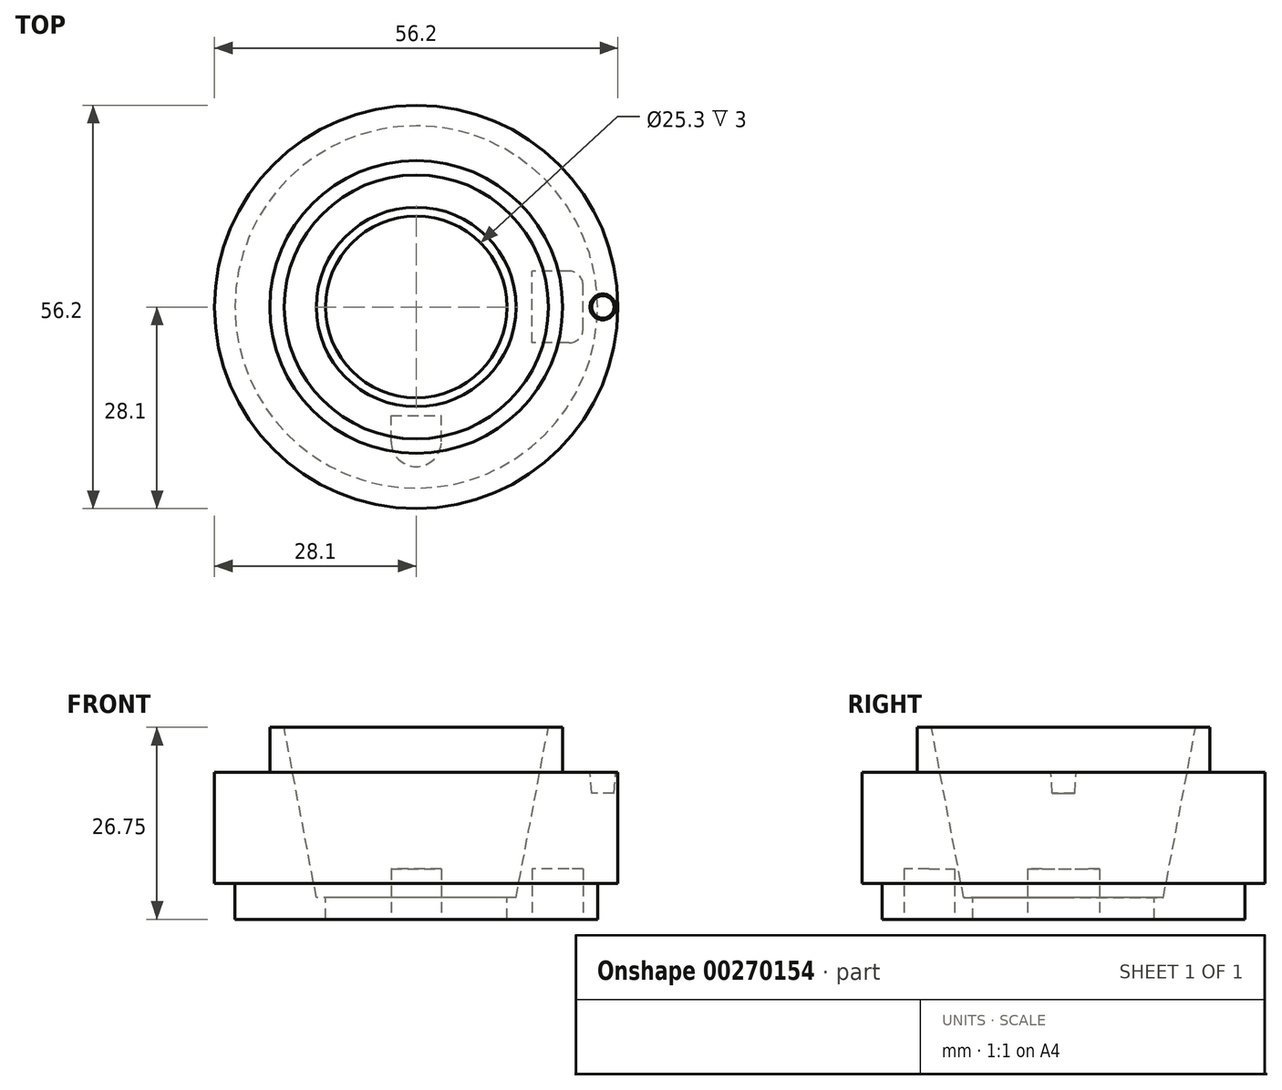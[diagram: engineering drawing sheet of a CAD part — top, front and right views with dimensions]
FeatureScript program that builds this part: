
annotation { "Feature Type Name" : "Feature", "Feature Type Description" : "" }
export const myFeature = defineFeature(function(context is Context, id is Id, definition is map)
    precondition{}
    {
        {
            var Q0;
            Q0=qCreatedBy(makeId("Front.planeOp"),FACE);
            var sketch = newSketch(context, id + "F0", { "sketchPlane" : qUnion([Q0])});
            skLineSegment(sketch, "E0", {"start": v(0, 18.35) * mm, "end": v(0, -26.13) * mm, "construction": true});
            skLineSegment(sketch, "E1", {"start": v(0, 0) * mm, "end": v(34.76, 0) * mm, "construction": true});
            skLineSegment(sketch, "E2", {"start": v(25.25, -40) * mm, "end": v(12.65, -40) * mm});
            skLineSegment(sketch, "E3", {"start": v(28.1, -19.5) * mm, "end": v(20.4, -19.5) * mm});
            skLineSegment(sketch, "E4", {"start": v(12.65, -40) * mm, "end": v(12.65, -37) * mm});
            skLineSegment(sketch, "E5", {"start": v(20.4, -19.5) * mm, "end": v(20.4, -13.25) * mm});
            skLineSegment(sketch, "E6", {"start": v(20.4, -13.25) * mm, "end": v(18.4, -13.25) * mm});
            skLineSegment(sketch, "E7", {"start": v(12.65, -37) * mm, "end": v(13.9, -37) * mm});
            skLineSegment(sketch, "E8", {"start": v(13.9, -37) * mm, "end": v(18.4, -13.25) * mm});
            skLineSegment(sketch, "E9", {"start": v(26, -10.98) * mm, "end": v(26, -23.61) * mm, "construction": true});
            skLineSegment(sketch, "E10", {"start": v(28.1, -19.5) * mm, "end": v(28.1, -35) * mm});
            skLineSegment(sketch, "E11", {"start": v(25.25, -40) * mm, "end": v(25.25, -35) * mm});
            skLineSegment(sketch, "E12", {"start": v(25.25, -35) * mm, "end": v(28.1, -35) * mm});
            skSolve(sketch);
        }
        {
            var Q0;
            Q0=makeQuery(id+"F0.imprint","IMPRINT",FACE,{"disambiguationData":[TD([[makeQuery(id+"F0.imprint","IMPRINT",EDGE,{"derivedFrom":sQuery(id+"F0.wireOp",EDGE,"E2")}),-1.0]])]});
            var Q1;
            Q1=sQuery(id+"F0.wireOp",EDGE,"E0");
            revolve(context, id + "F1", {"entities" : qUnion([Q0]), "axis" : qUnion([Q1]), "revolveType" : RevolveType.FULL});
        }
        {
            var Q0;
            Q0=makeQuery(id+"F1.opRevolve","SWEPT_FACE",FACE,{"disambiguationData":[OSD([sQuery(id+"F0.wireOp",EDGE,"E3")])]});
            var sketch = newSketch(context, id + "F2", { "sketchPlane" : qUnion([Q0])});
            skCircle(sketch, "E13", {"center": v(0, 0) * mm, "radius": 26 * mm, "construction": true});
            skPoint(sketch, "E14", {"position": v(0, -26) * mm});
            skPoint(sketch, "E15", {"position": v(26, 0) * mm});
            skPoint(sketch, "E16", {"position": v(-26, 0) * mm});
            skPoint(sketch, "E17", {"position": v(0, 26) * mm});
            skSolve(sketch);
        }
        {
            var Q0;
            Q0=qCreatedBy(makeId("Front.planeOp"),FACE);
            var sketch = newSketch(context, id + "F3", { "sketchPlane" : qUnion([Q0])});
            skLineSegment(sketch, "E18.0", {"start": v(26, -19.5) * mm, "end": v(27.8, -19.5) * mm});
            skLineSegment(sketch, "E19", {"start": v(27.8, -19.5) * mm, "end": v(27.56, -22.42) * mm});
            skLineSegment(sketch, "E20", {"start": v(27.56, -22.42) * mm, "end": v(26, -22.42) * mm});
            skLineSegment(sketch, "E21", {"start": v(26, -22.42) * mm, "end": v(26, -19.5) * mm});
            skPoint(sketch, "E22.orphan", {"position": v(-28.1, -19.5) * mm});
            skPoint(sketch, "E23.orphan", {"position": v(28.1, -19.5) * mm});
            skSolve(sketch);
        }
        {
            var Q0;
            Q0 = qSketchRegion(id + "F3", true);
            var Q1;
            Q1=sQuery(id+"F3.wireOp",EDGE,"E21");
            revolve(context, id + "F4", {"operationType" : NewBodyOperationType.REMOVE, "entities" : qUnion([Q0]), "axis" : qUnion([Q1]), "revolveType" : RevolveType.FULL, "oppositeDirection" : true});
        }
        {
            var Q0;
            Q0=makeQuery(id+"F1.opRevolve","SWEPT_FACE",FACE,{"disambiguationData":[OSD([sQuery(id+"F0.wireOp",EDGE,"E2")])]});
            var sketch = newSketch(context, id + "F5", { "sketchPlane" : qUnion([Q0])});
            skLineSegment(sketch, "E24.bottom", {"start": v(21.25, 5) * mm, "end": v(16.15, 5) * mm});
            skLineSegment(sketch, "E24.top", {"start": v(21.25, -5) * mm, "end": v(16.15, -5) * mm});
            skLineSegment(sketch, "E24.left", {"start": v(23.25, 3) * mm, "end": v(23.25, -3) * mm});
            skLineSegment(sketch, "E24.right", {"start": v(16.15, 5) * mm, "end": v(16.15, -5) * mm});
            skLineSegment(sketch, "E25.bottom", {"start": v(0, 22.25) * mm, "end": v(0, 22.25) * mm});
            skLineSegment(sketch, "E25.top", {"start": v(-3.5, 15.15) * mm, "end": v(3.5, 15.15) * mm});
            skLineSegment(sketch, "E25.left", {"start": v(-3.5, 18.75) * mm, "end": v(-3.5, 15.15) * mm});
            skLineSegment(sketch, "E25.right", {"start": v(3.5, 18.75) * mm, "end": v(3.5, 15.15) * mm});
            skPoint(sketch, "E26.visualSharp", {"position": v(23.25, 5) * mm});
            skArc(sketch, "E26.filletArc", {"start": v(23.25, 3) * mm, "mid": v(22.66, 4.41) * mm, "end": v(21.25, 5) * mm});
            skPoint(sketch, "E27.visualSharp", {"position": v(23.25, -5) * mm});
            skArc(sketch, "E27.filletArc", {"start": v(21.25, -5) * mm, "mid": v(22.66, -4.41) * mm, "end": v(23.25, -3) * mm});
            skPoint(sketch, "E28.visualSharp", {"position": v(-3.5, 22.25) * mm});
            skArc(sketch, "E28.filletArc", {"start": v(0, 22.25) * mm, "mid": v(-2.47, 21.22) * mm, "end": v(-3.5, 18.75) * mm});
            skPoint(sketch, "E29.visualSharp", {"position": v(3.5, 22.25) * mm});
            skArc(sketch, "E29.filletArc", {"start": v(3.5, 18.75) * mm, "mid": v(2.47, 21.22) * mm, "end": v(0, 22.25) * mm});
            skSolve(sketch);
        }
        {
            var Q0;
            Q0=makeQuery(id+"F5.imprint","IMPRINT",FACE,{"disambiguationData":[TD([[makeQuery(id+"F5.imprint","IMPRINT",EDGE,{"derivedFrom":sQuery(id+"F5.wireOp",EDGE,"E25.top")}),1.0]])]});
            var Q1;
            Q1=makeQuery(id+"F5.imprint","IMPRINT",FACE,{"disambiguationData":[TD([[makeQuery(id+"F5.imprint","IMPRINT",EDGE,{"derivedFrom":sQuery(id+"F5.wireOp",EDGE,"E24.bottom")}),1.0]])]});
            extrude(context, id + "F6", {"entities" : qUnion([Q0, Q1]), "operationType" : NewBodyOperationType.REMOVE, "oppositeDirection" : true, "depth" : 7 * mm});
        }
    });
